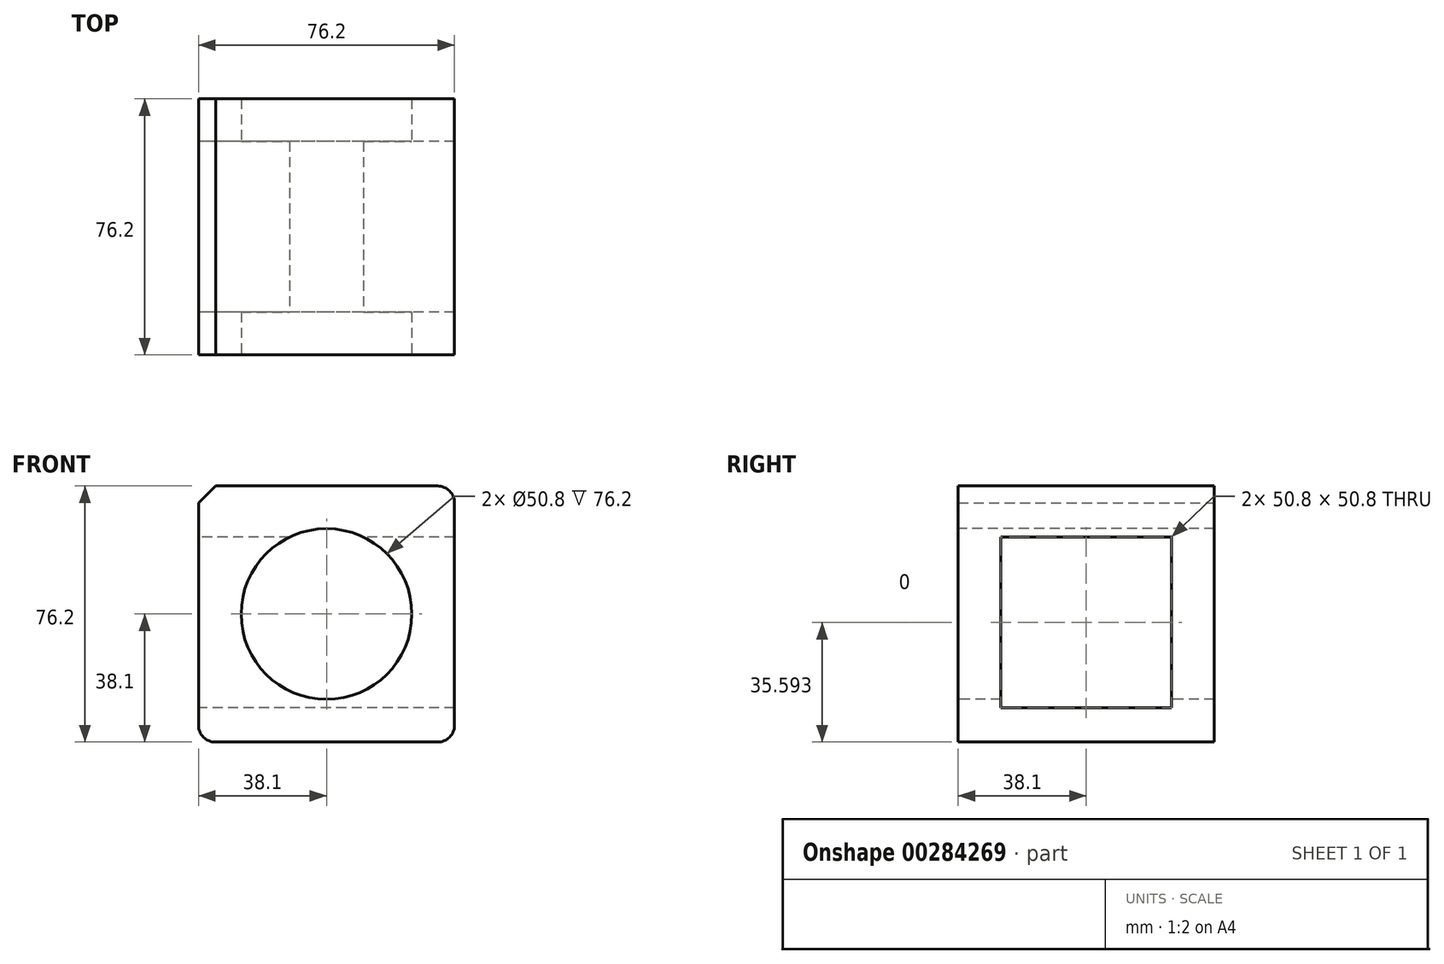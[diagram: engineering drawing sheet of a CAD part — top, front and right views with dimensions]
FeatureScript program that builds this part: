
annotation { "Feature Type Name" : "Feature", "Feature Type Description" : "" }
export const myFeature = defineFeature(function(context is Context, id is Id, definition is map)
    precondition{}
    {
        {
            var Q0;
            Q0=qCreatedBy(makeId("Front.planeOp"),FACE);
            var sketch = newSketch(context, id + "F0", { "sketchPlane" : qUnion([Q0])});
            skLineSegment(sketch, "E0.bottom", {"start": v(38.1, 38.1) * mm, "end": v(-38.1, 38.1) * mm});
            skLineSegment(sketch, "E0.top", {"start": v(38.1, -38.1) * mm, "end": v(-38.1, -38.1) * mm});
            skLineSegment(sketch, "E0.left", {"start": v(38.1, 38.1) * mm, "end": v(38.1, -38.1) * mm});
            skLineSegment(sketch, "E0.right", {"start": v(-38.1, 38.1) * mm, "end": v(-38.1, -38.1) * mm});
            skPoint(sketch, "E0.middle", {"position": v(0, 0) * mm});
            skSolve(sketch);
        }
        {
            var Q0;
            Q0 = qSketchRegion(id + "F0", true);
            extrude(context, id + "F1", {"entities" : qUnion([Q0]), "endBound" : BoundingType.SYMMETRIC, "depth" : 76.2 * mm});
        }
        {
            var Q0;
            Q0=makeQuery(id+"F1.opExtrude","CAP_FACE",FACE,{"disambiguationData":[OSD([sQuery(id+"F0.wireOp",EDGE,"E0.bottom"),sQuery(id+"F0.wireOp",EDGE,"E0.top"),sQuery(id+"F0.wireOp",EDGE,"E0.left"),sQuery(id+"F0.wireOp",EDGE,"E0.right")])],"isStart":false});
            var sketch = newSketch(context, id + "F2", { "sketchPlane" : qUnion([Q0])});
            skCircle(sketch, "E1", {"center": v(0, 0) * mm, "radius": 25.4 * mm});
            skSolve(sketch);
        }
        {
            var Q0;
            Q0=makeQuery(id+"F2.imprint","IMPRINT",FACE,{"disambiguationData":[TD([[makeQuery(id+"F2.imprint","IMPRINT",EDGE,{"derivedFrom":sQuery(id+"F2.wireOp",EDGE,"E1")}),1.0]])]});
            extrude(context, id + "F3", {"entities" : qUnion([Q0]), "operationType" : NewBodyOperationType.REMOVE, "oppositeDirection" : true, "depth" : 76.2 * mm});
        }
        {
            var Q0;
            Q0=makeQuery(id+"F1.opExtrude","SWEPT_EDGE",EDGE,{"disambiguationData":[OSD([sQuery(id+"F0.wireOp",EDGE,"E0.bottom"),sQuery(id+"F0.wireOp",EDGE,"E0.left")])]});
            fillet(context, id + "F4", {"entities" : qUnion([Q0]), "radius" : 5.08 * mm, "tangentPropagation" : true, "allowEdgeOverflow" : false});
        }
        {
            var Q0;
            Q0=makeQuery(id+"F1.opExtrude","SWEPT_EDGE",EDGE,{"disambiguationData":[OSD([sQuery(id+"F0.wireOp",EDGE,"E0.bottom"),sQuery(id+"F0.wireOp",EDGE,"E0.right")])]});
            chamfer(context, id + "F5", {"entities" : qUnion([Q0]), "width" : 5.08 * mm, "tangentPropagation" : true});
        }
        {
            var Q0;
            Q0=makeQuery(id+"F1.opExtrude","SWEPT_EDGE",EDGE,{"disambiguationData":[OSD([sQuery(id+"F0.wireOp",EDGE,"E0.top"),sQuery(id+"F0.wireOp",EDGE,"E0.left")])]});
            fillet(context, id + "F6", {"entities" : qUnion([Q0]), "radius" : 5.08 * mm, "tangentPropagation" : true, "allowEdgeOverflow" : false});
        }
        {
            var Q0;
            Q0=makeQuery(id+"F1.opExtrude","SWEPT_EDGE",EDGE,{"disambiguationData":[OSD([sQuery(id+"F0.wireOp",EDGE,"E0.top"),sQuery(id+"F0.wireOp",EDGE,"E0.right")])]});
            fillet(context, id + "F7", {"entities" : qUnion([Q0]), "radius" : 5.08 * mm, "tangentPropagation" : true, "allowEdgeOverflow" : false});
        }
        {
            var Q0;
            Q0=makeQuery(id+"F1.opExtrude","SWEPT_FACE",FACE,{"disambiguationData":[OSD([sQuery(id+"F0.wireOp",EDGE,"E0.right")])]});
            var sketch = newSketch(context, id + "F8", { "sketchPlane" : qUnion([Q0])});
            skLineSegment(sketch, "E2.bottom", {"start": v(25.4, 22.9) * mm, "end": v(-25.4, 22.9) * mm});
            skLineSegment(sketch, "E2.top", {"start": v(25.4, -27.9) * mm, "end": v(-25.4, -27.9) * mm});
            skLineSegment(sketch, "E2.left", {"start": v(25.4, 22.9) * mm, "end": v(25.4, -27.9) * mm});
            skLineSegment(sketch, "E2.right", {"start": v(-25.4, 22.9) * mm, "end": v(-25.4, -27.9) * mm});
            skPoint(sketch, "E2.middle", {"position": v(0, -2.5) * mm});
            skSolve(sketch);
        }
        {
            var Q0;
            Q0 = qSketchRegion(id + "F8", true);
            extrude(context, id + "F9", {"entities" : qUnion([Q0]), "operationType" : NewBodyOperationType.REMOVE, "oppositeDirection" : true, "depth" : 76.2 * mm});
        }
    });
